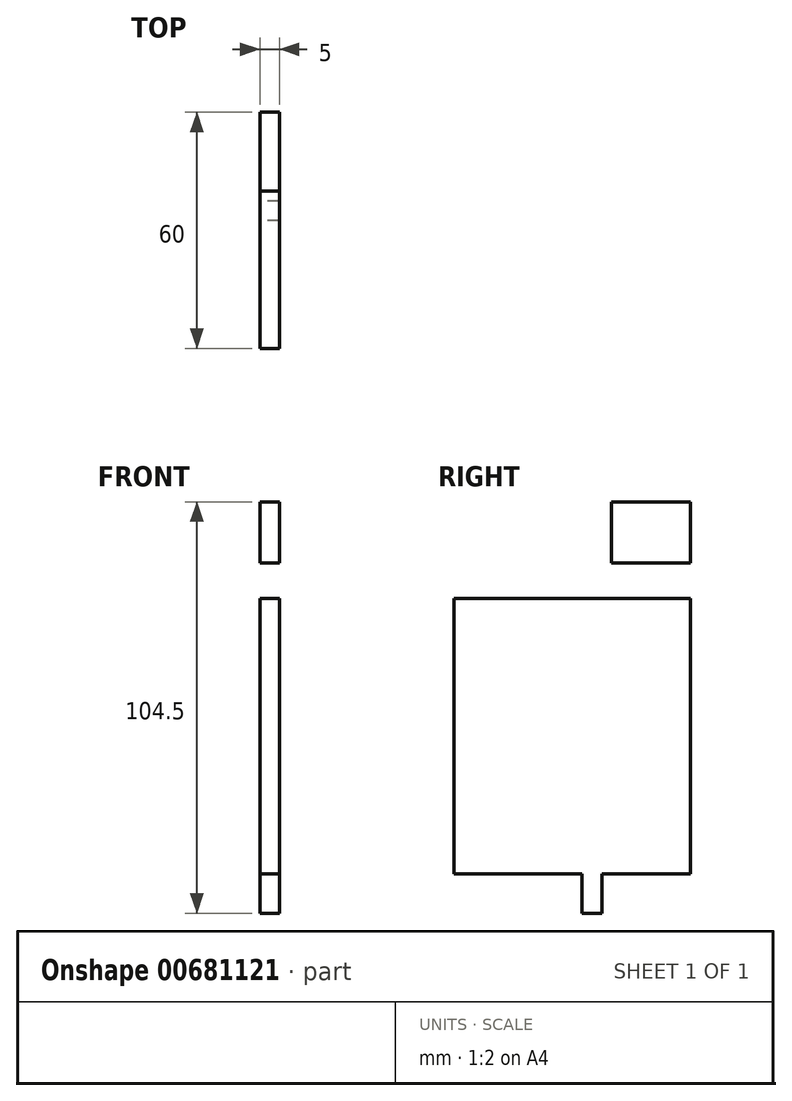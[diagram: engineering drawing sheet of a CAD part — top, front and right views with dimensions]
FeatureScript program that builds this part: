
annotation { "Feature Type Name" : "Feature", "Feature Type Description" : "" }
export const myFeature = defineFeature(function(context is Context, id is Id, definition is map)
    precondition{}
    {
        {
            var Q0;
            Q0=qCreatedBy(makeId("Right.planeOp"),FACE);
            var sketch = newSketch(context, id + "F0", { "sketchPlane" : qUnion([Q0])});
            skLineSegment(sketch, "E0", {"start": v(0, 0) * mm, "end": v(0, -70) * mm});
            skLineSegment(sketch, "E1", {"start": v(0, -70) * mm, "end": v(12.4, -70) * mm});
            skLineSegment(sketch, "E2.0", {"start": v(37.5, -70.04) * mm, "end": v(37.5, -81.07) * mm});
            skLineSegment(sketch, "E3", {"start": v(12, -70) * mm, "end": v(12.4, -70) * mm});
            skLineSegment(sketch, "E4", {"start": v(0, -70) * mm, "end": v(12, -70) * mm});
            skLineSegment(sketch, "E5", {"start": v(32.5, -80) * mm, "end": v(32.5, -70) * mm});
            skPoint(sketch, "E6.trimOffspring.start.orphan", {"position": v(25, -70) * mm});
            skLineSegment(sketch, "E7", {"start": v(37.5, -80) * mm, "end": v(37.5, -81.07) * mm});
            skLineSegment(sketch, "E8", {"start": v(32.5, -80) * mm, "end": v(37.5, -80) * mm});
            skLineSegment(sketch, "E9", {"start": v(11.37, -27.14) * mm, "end": v(11.37, -26.74) * mm});
            skLineSegment(sketch, "E10", {"start": v(38.63, -27.14) * mm, "end": v(38.63, -26.74) * mm});
            skLineSegment(sketch, "E11", {"start": v(0, -70) * mm, "end": v(32.5, -70) * mm});
            skLineSegment(sketch, "E12.trimOffspring", {"start": v(32.5, -70) * mm, "end": v(0, -70) * mm});
            skLineSegment(sketch, "E13.0", {"start": v(60, -0.04) * mm, "end": v(60, -70.04) * mm});
            skLineSegment(sketch, "E14", {"start": v(60, -70.04) * mm, "end": v(37.5, -70.04) * mm});
            skLineSegment(sketch, "E15.0", {"start": v(42.5, 9) * mm, "end": v(40, 9) * mm});
            skPoint(sketch, "E16.orphan", {"position": v(42.5, 0) * mm});
            skLineSegment(sketch, "E17", {"start": v(40, 24.5) * mm, "end": v(42.5, 24.5) * mm});
            skPoint(sketch, "E17.startSnap0", {"position": v(42.5, 24.5) * mm});
            skPoint(sketch, "E17.endSnap0", {"position": v(42.5, 24.5) * mm});
            skPoint(sketch, "E18.end.orphan", {"position": v(42.5, 40) * mm});
            skLineSegment(sketch, "E19", {"start": v(60, 9) * mm, "end": v(60, 24.5) * mm});
            skLineSegment(sketch, "E20", {"start": v(42.5, 24.5) * mm, "end": v(60, 24.5) * mm});
            skLineSegment(sketch, "E21", {"start": v(42.5, 9) * mm, "end": v(60, 9) * mm});
            skPoint(sketch, "E22.orphan", {"position": v(22.5, 24.5) * mm});
            skLineSegment(sketch, "E23.0", {"start": v(40, 9) * mm, "end": v(40, 24.5) * mm});
            skLineSegment(sketch, "E24", {"start": v(0, 0) * mm, "end": v(60, -0.04) * mm});
            skSolve(sketch);
        }
        {
            var Q0;
            {var subQ1=sQuery(id+"F0.wireOp",EDGE,"E0");Q0=makeQuery(id+"F0.imprint","IMPRINT",FACE,{"disambiguationData":[TD([[makeQuery(id+"F0.imprint","IMPRINT",EDGE,{"derivedFrom":subQ1}),1.0]])]});}
            var Q1;
            Q1=makeQuery(id+"F0.imprint","IMPRINT",FACE,{"disambiguationData":[TD([[makeQuery(id+"F0.imprint","IMPRINT",EDGE,{"derivedFrom":sQuery(id+"F0.wireOp",EDGE,"KUJi0EKv-68yc-6Nkf-644W-VpfIH1upkmh2")}),-1.0]])]});
            var Q2;
            Q2=makeQuery(id+"F0.imprint","IMPRINT",FACE,{"disambiguationData":[TD([[makeQuery(id+"F0.imprint","IMPRINT",EDGE,{"derivedFrom":sQuery(id+"F0.wireOp",EDGE,"E15.0")}),-1.0]])]});
            extrude(context, id + "F1", {"entities" : qUnion([Q0, Q1, Q2]), "depth" : 5 * mm, "offsetDistance" : 25 * mm});
        }
    });
